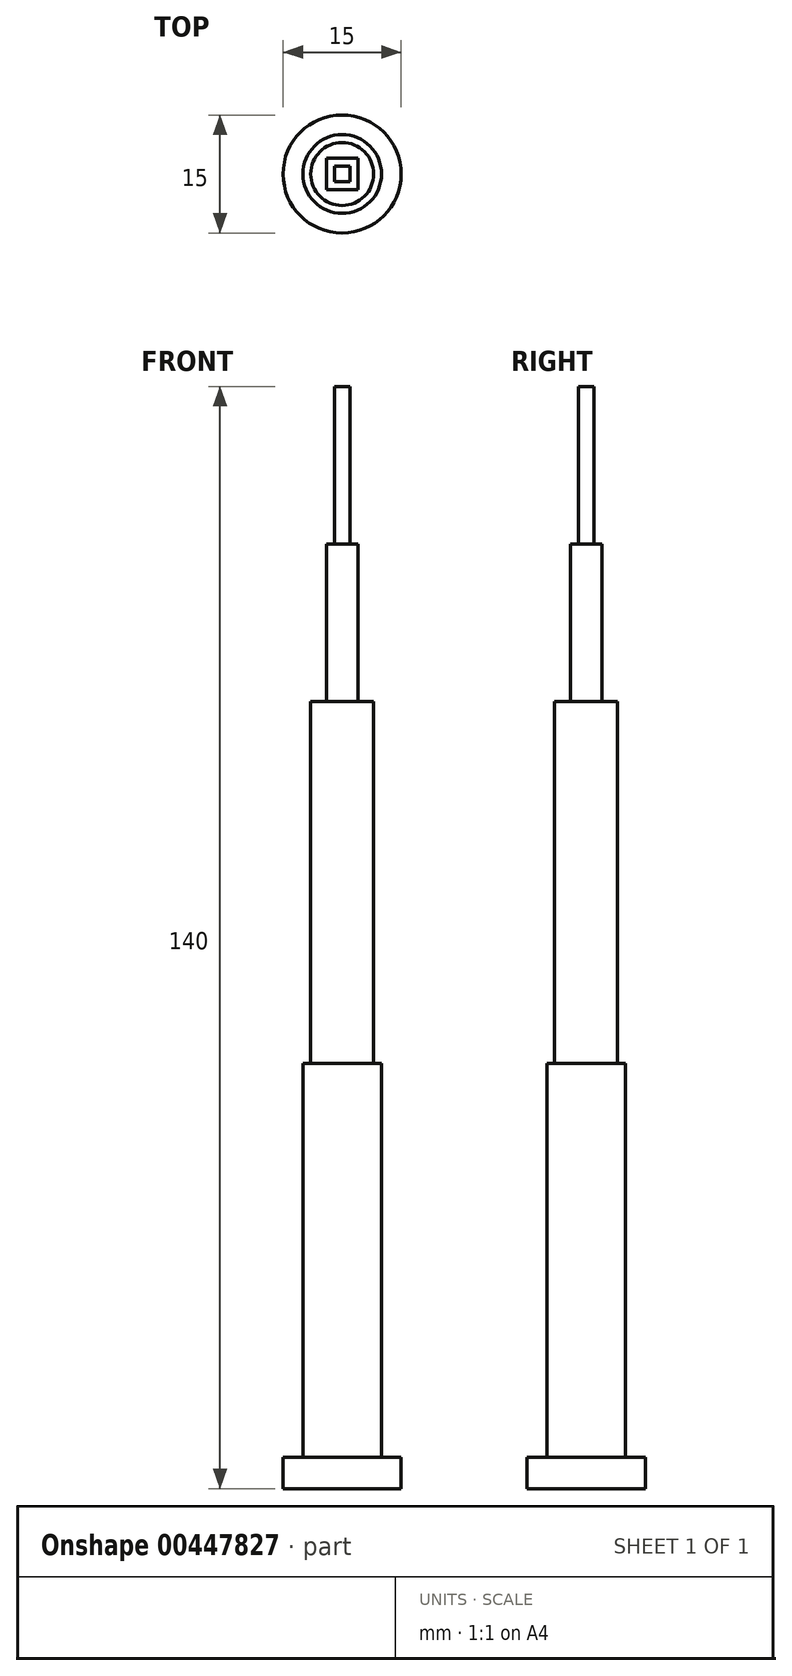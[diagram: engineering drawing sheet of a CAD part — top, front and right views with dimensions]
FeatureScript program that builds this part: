
annotation { "Feature Type Name" : "Feature", "Feature Type Description" : "" }
export const myFeature = defineFeature(function(context is Context, id is Id, definition is map)
    precondition{}
    {
        {
            var Q0;
            Q0=qCreatedBy(makeId("Top.planeOp"),FACE);
            var sketch = newSketch(context, id + "F0", { "sketchPlane" : qUnion([Q0])});
            skCircle(sketch, "E0", {"center": v(0, 0) * mm, "radius": 7.5 * mm});
            skSolve(sketch);
        }
        {
            var Q0;
            Q0=qSketchRegion(id+"F0",true);
            extrude(context, id + "F1", {"entities" : qUnion([Q0]), "depth" : 4 * mm});
        }
        {
            var Q0;
            Q0=qCreatedBy(makeId("Top.planeOp"),FACE);
            var sketch = newSketch(context, id + "F2", { "sketchPlane" : qUnion([Q0])});
            skCircle(sketch, "E1", {"center": v(0, 0) * mm, "radius": 5 * mm});
            skSolve(sketch);
        }
        {
            var Q0;
            Q0=qSketchRegion(id+"F2",true);
            extrude(context, id + "F3", {"entities" : qUnion([Q0]), "operationType" : NewBodyOperationType.ADD, "depth" : 54 * mm});
        }
        {
            var Q0;
            Q0=makeQuery(id+"F3.opExtrude","CAP_FACE",FACE,{"disambiguationData":[OSD([sQuery(id+"F2.wireOp",EDGE,"E1")])],"isStart":false});
            var sketch = newSketch(context, id + "F4", { "sketchPlane" : qUnion([Q0])});
            skCircle(sketch, "E2", {"center": v(0, 0) * mm, "radius": 4 * mm});
            skSolve(sketch);
        }
        {
            var Q0;
            Q0=qSketchRegion(id+"F4",true);
            extrude(context, id + "F5", {"entities" : qUnion([Q0]), "operationType" : NewBodyOperationType.ADD, "depth" : 46 * mm});
        }
        {
            var Q0;
            Q0=makeQuery(id+"F5.opExtrude","CAP_FACE",FACE,{"disambiguationData":[OSD([sQuery(id+"F4.wireOp",EDGE,"E2")])],"isStart":false});
            var sketch = newSketch(context, id + "F6", { "sketchPlane" : qUnion([Q0])});
            skLineSegment(sketch, "E3.bottom", {"start": v(-2, 2) * mm, "end": v(2, 2) * mm});
            skLineSegment(sketch, "E3.top", {"start": v(-2, -2) * mm, "end": v(2, -2) * mm});
            skLineSegment(sketch, "E3.left", {"start": v(-2, 2) * mm, "end": v(-2, -2) * mm});
            skLineSegment(sketch, "E3.right", {"start": v(2, 2) * mm, "end": v(2, -2) * mm});
            skSolve(sketch);
        }
        {
            var Q0;
            Q0=qSketchRegion(id+"F6",true);
            extrude(context, id + "F7", {"entities" : qUnion([Q0]), "operationType" : NewBodyOperationType.ADD, "depth" : 20 * mm});
        }
        {
            var Q0;
            Q0=makeQuery(id+"F7.opExtrude","CAP_FACE",FACE,{"disambiguationData":[OSD([sQuery(id+"F6.wireOp",EDGE,"E3.bottom"),sQuery(id+"F6.wireOp",EDGE,"E3.top"),sQuery(id+"F6.wireOp",EDGE,"E3.left"),sQuery(id+"F6.wireOp",EDGE,"E3.right")])],"isStart":false});
            var sketch = newSketch(context, id + "F8", { "sketchPlane" : qUnion([Q0])});
            skLineSegment(sketch, "E4.bottom", {"start": v(-1, 1) * mm, "end": v(1, 1) * mm});
            skLineSegment(sketch, "E4.top", {"start": v(-1, -1) * mm, "end": v(1, -1) * mm});
            skLineSegment(sketch, "E4.left", {"start": v(-1, 1) * mm, "end": v(-1, -1) * mm});
            skLineSegment(sketch, "E4.right", {"start": v(1, 1) * mm, "end": v(1, -1) * mm});
            skSolve(sketch);
        }
        {
            var Q0;
            Q0 = qSketchRegion(id + "F8", true);
            extrude(context, id + "F9", {"entities" : qUnion([Q0]), "operationType" : NewBodyOperationType.ADD, "depth" : 20 * mm});
        }
    });
